# Revit family: IS_Joy_BC777_BIM_GB
name_source: partatom
category: Plumbing Fixtures
revit_build: Autodesk Revit 2017 (Build: 20160225_1515(x64)
units: mm (PartAtom-declared; Revit-internal decimal feet)

## family parameters
Always vertical = No
Cut with Voids When Loaded = No
OmniClass Number = 23.45.55.17
OmniClass Title = Mixing Faucets
Part Type = Normal
Room Calculation Point = No
Round Connector Dimension = Use Diameter
Shared = No
Work Plane-Based = No

## types (4) — shared parameters
Accessories = https://www.idealstandard.co.uk
AssetType = Fixed
BIMObjectName = ISI_IdealStandard_Washbasin manual water supply sets_Joy_BC777
BarCode = 3800861086840
Brand = Ideal Standard
CurrencyUnit = £
Description = JOY Single lever basin mixer, embossed with high spout and 169mm projection. Available in four different finishes, Chrome (AA), Silver storm (GN) 386, Brushed gold (A2) and Magnetic grey (A5)
DistributedBy = Ideal Standard
DurationUnit = Years
ExpectedLife = 30
FaucetFunction = MIXED
FaucetOperation = OTHER
FaucetType = OTHER
Features = Single lever basin mixer, embossed with high spout and 169mm projection. Available in four different finishes, Chrome (AA), Silver storm (GN) 386, Brushed gold (A2) and Magnetic grey (A5)
Help = https://www.idealstandard.co.uk
IfcExportAs = IfcValveType
IfcExportType = FAUCET
Installation instructions = https://www.idealspec.co.uk
InstallationInstructions = https://www.idealstandard.co.uk
IsBuiltIn = No
MaintenanceInformation = https://www.idealstandard.co.uk
Manufacturer = Ideal Standard
ManufacturerURL = https://www.idealstandard.co.uk
Material = Brass
ModelNumber = BC777
NBS Reference Code = 45-35-70/371
NBS Reference Description = Water supply fittings for wash basins and troughs
Name = Washbasin manual water supply sets_Joy_BC777_IdealStandard
NettWeight = 1.63
NominalDepth = 405 mm
NominalHeight = 90 mm  [stored 0.295276 ft]
NominalLength = 405 mm
NominalWidth = 215 mm
Product certification = https://www.idealstandard.co.uk
Product group = BASIN MIXER
ProductInformation = https://www.idealspec.co.uk
Shape = Sculptured
Size = 105 x 230 x 311 mm
Space = Internal
SpareParts = https://www.idealspec.co.uk
SustainabilityPerformance = https://www.idealspec.co.uk
TestPressure = 10 Bar
URL = https://www.idealstandard.co.uk
Uniclass 2015 Code = Pr_40_20_87_96
Uniclass 2015 Name = Washbasin manual water supply sets
Uniclass2015Code = Pr_40_20_87_96
Uniclass2015Title = Washbasin manual water supply sets
Uniclass2015Version = v1.1
Version = 1
VolumeUnits = Litres
WRASURL = https://www.wras.co.uk
WarrantyDescription = Manufacturers Warranty
WarrantyDurationParts = 5
WarrantyDurationUnit = year
WarrantyGuarantorParts = https://www.idealspec.co.uk
WorkingPressure = 3bar
zero-valued in all types: InletConnectionSize, MaterialThickness

## per-type parameters (varying)
| type | Color | Finish | MainColor | Model | ModelReference |
| BC777A2 - JOY HIGH SPT BSN R-MTD 5L PUW/M BR GOLD | Brushed Gold | Brushed Gold | Brushed Gold | BC777A2 | BC777A2 |
| BC777A5 - JOY HIGH SPT BSN R-MTD 5L PUW/M MGN GREY | Magnetic grey | Magnetic grey | Magnetic grey | BC777A5 | BC777A5 |
| BC777AA - JOY BSN MXR R-MTD 5L NO PUW CHR | Chrome | Chrome | Chrome | BC777AA | BC777AA |
| BC777GN - JOY HIGH SPT BSN R-MTD 5L PUW/M SILV STORM | Silver storm | Silver storm | Silver storm | BC777GN | BC777GN |

note: [stored X ft] marks values corroborated as IEEE doubles in the binary element streams (Revit-internal decimal feet)

## geometry (parser evidence)
native form markers: Sweep x2
no freeform markers — native parametric forms only
